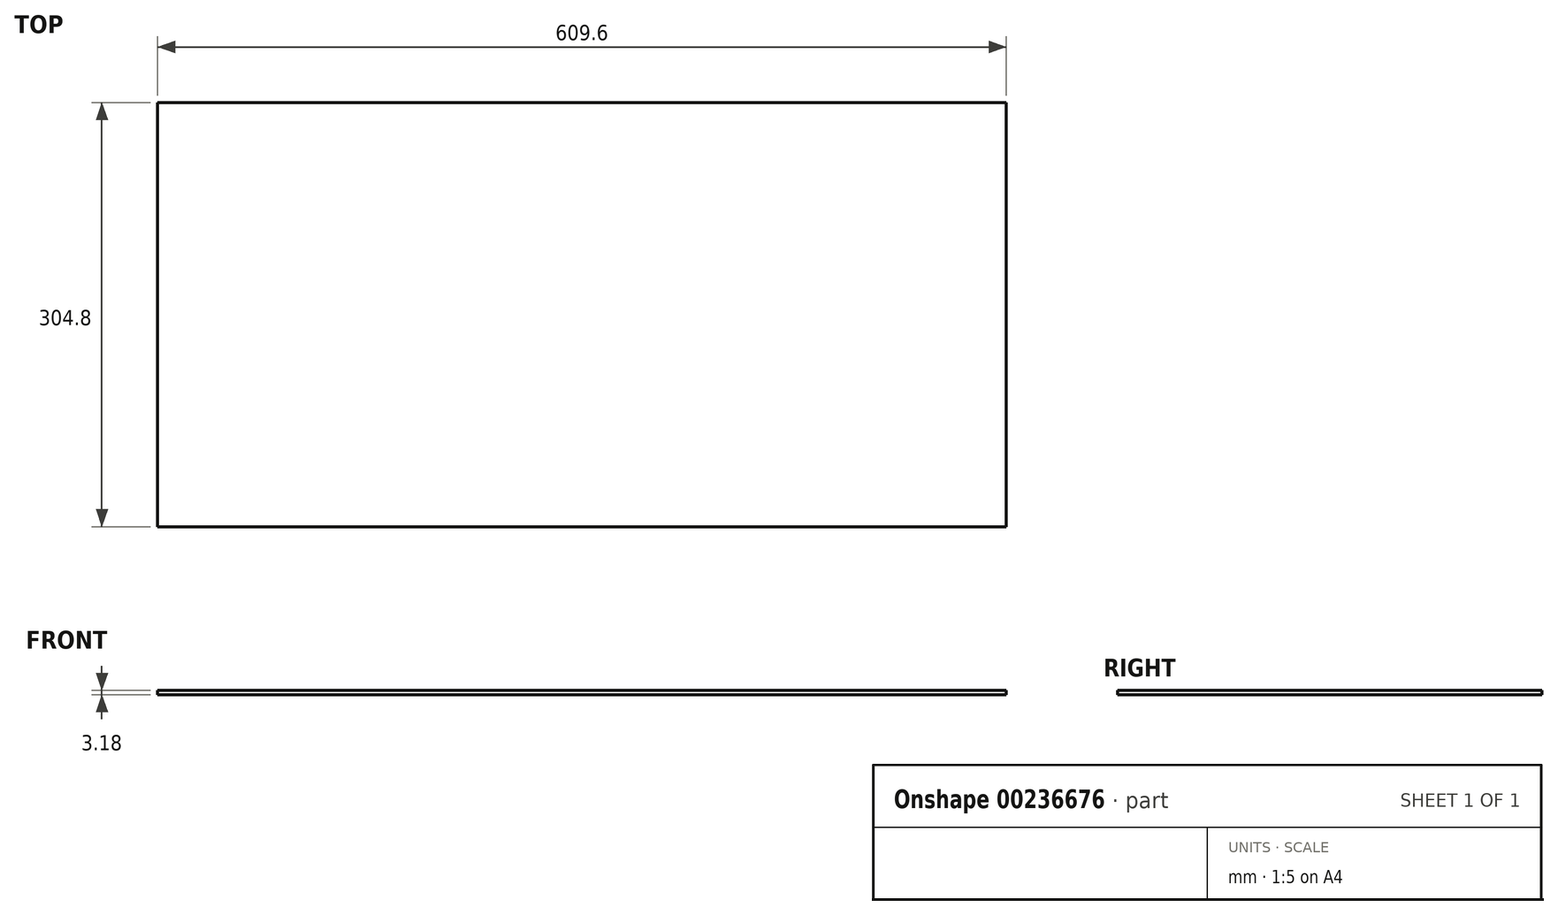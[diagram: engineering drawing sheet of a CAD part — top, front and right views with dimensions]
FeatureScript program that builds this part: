
annotation { "Feature Type Name" : "Feature", "Feature Type Description" : "" }
export const myFeature = defineFeature(function(context is Context, id is Id, definition is map)
    precondition{}
    {
        {
            var Q0;
            Q0=qCreatedBy(makeId("Top.planeOp"),FACE);
            var sketch = newSketch(context, id + "F0", { "sketchPlane" : qUnion([Q0])});
            skLineSegment(sketch, "E0.bottom", {"start": v(304.8, -152.4) * mm, "end": v(-304.8, -152.4) * mm});
            skLineSegment(sketch, "E0.top", {"start": v(304.8, 152.4) * mm, "end": v(-304.8, 152.4) * mm});
            skLineSegment(sketch, "E0.left", {"start": v(304.8, -152.4) * mm, "end": v(304.8, 152.4) * mm});
            skLineSegment(sketch, "E0.right", {"start": v(-304.8, -152.4) * mm, "end": v(-304.8, 152.4) * mm});
            skPoint(sketch, "E0.middle", {"position": v(0, 0) * mm});
            skSolve(sketch);
        }
        {
            var Q0;
            Q0 = qSketchRegion(id + "F0", true);
            extrude(context, id + "F1", {"entities" : qUnion([Q0]), "endBound" : BoundingType.SYMMETRIC, "depth" : 3.17 * mm});
        }
    });
